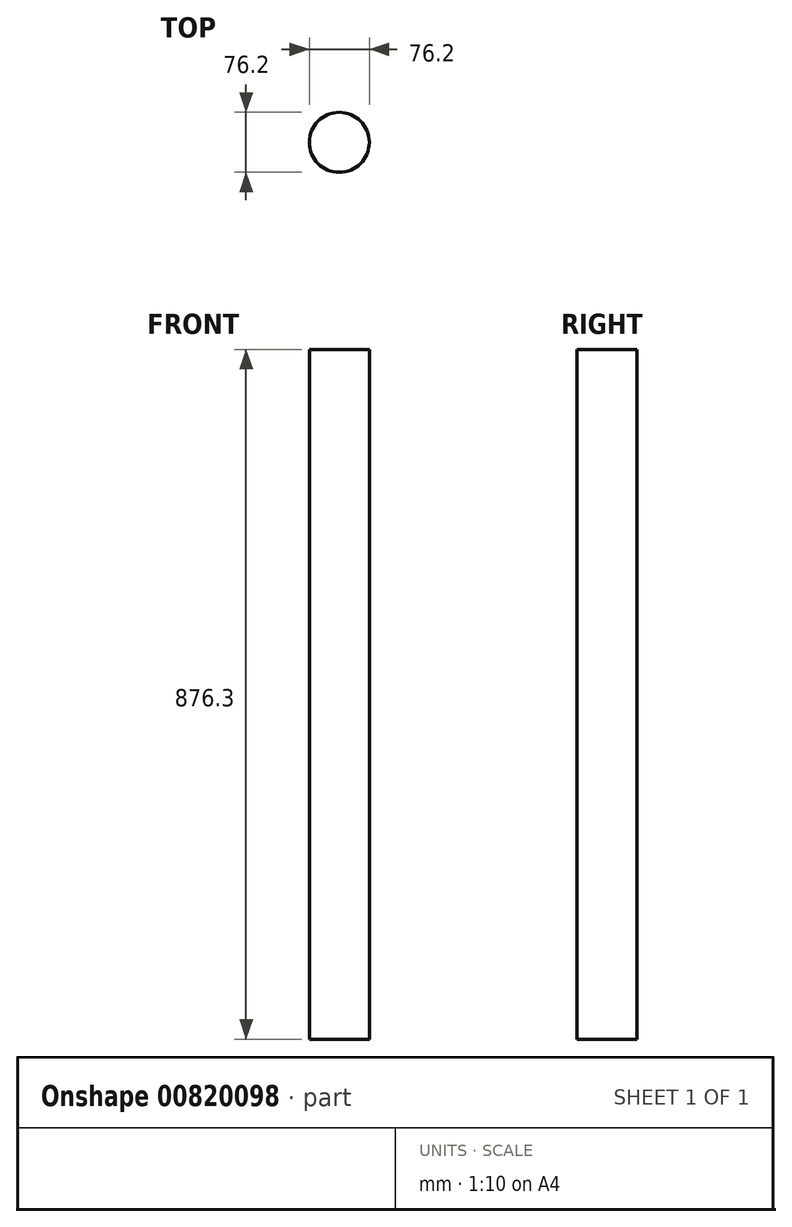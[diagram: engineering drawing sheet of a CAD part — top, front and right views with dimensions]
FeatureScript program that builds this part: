
annotation { "Feature Type Name" : "Feature", "Feature Type Description" : "" }
export const myFeature = defineFeature(function(context is Context, id is Id, definition is map)
    precondition{}
    {
        {
            var Q0;
            Q0=qCreatedBy(makeId("Top.planeOp"),FACE);
            var sketch = newSketch(context, id + "F0", { "sketchPlane" : qUnion([Q0])});
            skCircle(sketch, "E0", {"center": v(0, 0) * mm, "radius": 38.1 * mm});
            skSolve(sketch);
        }
        {
            var Q0;
            Q0 = qSketchRegion(id + "F0", true);
            extrude(context, id + "F1", {"entities" : qUnion([Q0]), "depth" : 876.3 * mm, "offsetDistance" : 25.4 * mm});
        }
    });
